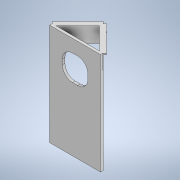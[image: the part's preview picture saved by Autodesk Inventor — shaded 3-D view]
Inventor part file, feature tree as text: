
AUTODESK INVENTOR PART (.ipt)
format: ipt  version: 2020 (Build 240168000, 168)  size: 163,840 bytes
history: native  units: mm
features: extrude x4, sketch x4
ambient origin geometry x8: Origin, YZ Plane, XZ Plane, XY Plane, X Axis, Y Axis, Z Axis, Center Point
bodies: Solid1 (feature_tree)
feature tree (8):
  extrude  "Extrusion1"  Depth=200.0mm
  extrude  "Extrusion2"  TaperAngle=45.0deg  [1 undecoded]
  extrude  "Extrusion6"  Depth=5.0mm
  extrude  "Extrusion9"  Depth=50.0mm
  sketch  "Sketch1"  dims[d0=100.0mm d1=200.0mm]
  sketch  "Sketch2"  dims[d2=5.0mm d3=0.0mm d4=45.0deg]
  sketch  "Sketch6"  dims[d5=5.0mm d6=5.0mm]
  sketch  "Sketch10"  dims[d7=30.0mm d8=0.0mm d21=50.0mm d22=50.0mm d23=20.0mm d24=5.0mm d25=0.0mm d33=5.0mm d34=5.0mm d36=3.0mm d37=0.0mm]
note: 1 required parameter value undecoded (feature->parameter linkage not recoverable at this tier; creation-order binding heuristic only, values carry confidence <= 0.55)
